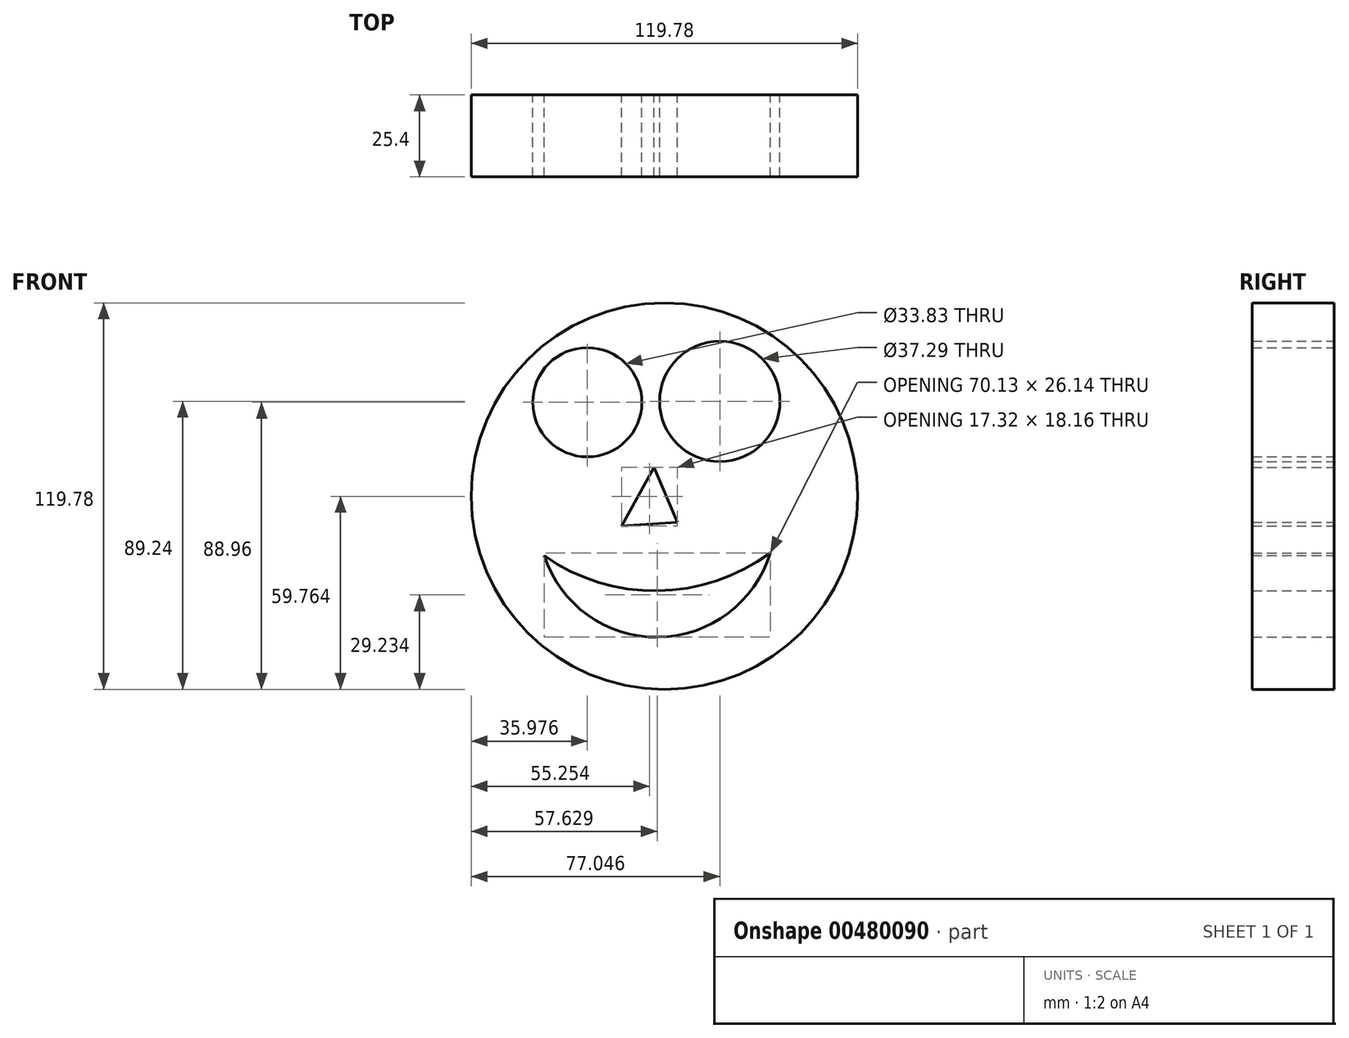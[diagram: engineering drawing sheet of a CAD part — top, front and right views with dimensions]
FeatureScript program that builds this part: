
annotation { "Feature Type Name" : "Feature", "Feature Type Description" : "" }
export const myFeature = defineFeature(function(context is Context, id is Id, definition is map)
    precondition{}
    {
        {
            var Q0;
            Q0=qCreatedBy(makeId("Front.planeOp"),FACE);
            var sketch = newSketch(context, id + "F0", { "sketchPlane" : qUnion([Q0])});
            skPoint(sketch, "E0.start.orphan", {"position": v(-72.29, 49.99) * mm});
            skPoint(sketch, "E1.start.orphan", {"position": v(-72.29, 51.15) * mm});
            skPoint(sketch, "E2.start.orphan", {"position": v(-72.29, 0) * mm});
            skCircle(sketch, "E3", {"center": v(0, 0) * mm, "radius": 59.89 * mm});
            skCircle(sketch, "E4", {"center": v(-23.91, 29.07) * mm, "radius": 16.91 * mm});
            skCircle(sketch, "E5", {"center": v(17.16, 29.35) * mm, "radius": 18.64 * mm});
            skArc(sketch, "E6", {"start": v(-37.32, -18.43) * mm, "mid": v(-1.95, -43.72) * mm, "end": v(32.8, -17.59) * mm});
            skLineSegment(sketch, "E7", {"start": v(-13.3, -9.2) * mm, "end": v(-3.24, 8.95) * mm});
            skLineSegment(sketch, "E8", {"start": v(-3.24, 8.95) * mm, "end": v(4.02, -8.09) * mm});
            skLineSegment(sketch, "E9", {"start": v(4.02, -8.09) * mm, "end": v(-13.3, -9.2) * mm});
            skArc(sketch, "E10", {"start": v(-37.32, -18.43) * mm, "mid": v(-2.13, -29.36) * mm, "end": v(32.8, -17.59) * mm});
            skSolve(sketch);
        }
        {
            var Q0;
            Q0 = qSketchRegion(id + "F0", true);
            extrude(context, id + "F1", {"entities" : qUnion([Q0]), "depth" : 25.4 * mm});
        }
    });
